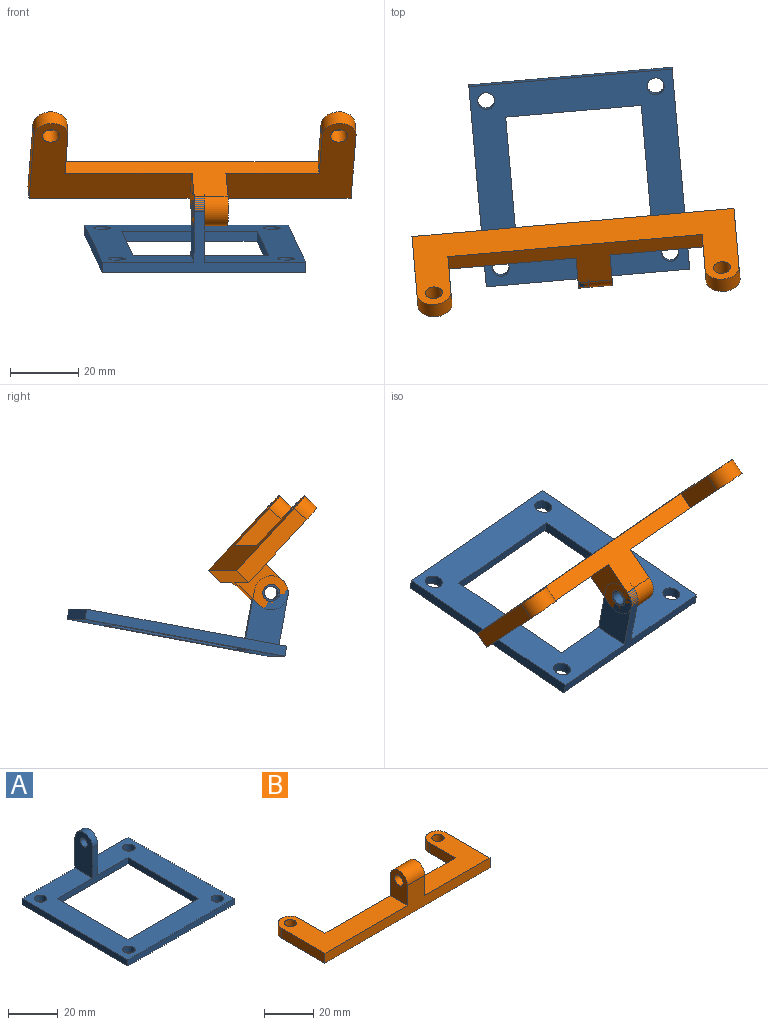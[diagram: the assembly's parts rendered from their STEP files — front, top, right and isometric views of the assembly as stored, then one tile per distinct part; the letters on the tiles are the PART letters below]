
ASSEMBLY  parts=2 mates=1
PART A: 18 faces, bbox 60x60x23 mm
  f0: plane 60x60mm, normal (0,0,1), area 1891.5mm2, adj f1,f2,f3,f4,f5,f6,f7,f8
  f1: plane 60x18mm, normal (0,1,0), area 225mm2, adj f0,f2,f8,f9,f10,f11,f12
  f2: plane 60x3mm, normal (-1,0,0), area 180mm2, adj f0,f1,f3,f9
  f3: plane 60x3mm, normal (0,-1,0), area 180mm2, adj f0,f2,f8,f9
  f4: plane 40x3mm, normal (1,0,0), area 120mm2, adj f0,f5,f7,f9
  f5: plane 40x18mm, normal (0,-1,0), area 165mm2, adj f0,f4,f6,f9,f10,f11,f12
  f6: plane 40x3mm, normal (-1,0,0), area 120mm2, adj f0,f5,f7,f9
  f7: plane 40x3mm, normal (0,1,0), area 120mm2, adj f0,f4,f6,f9
  f8: plane 60x3mm, normal (1,0,0), area 180mm2, adj f0,f1,f3,f9
  f9: plane 60x60mm, normal (0,0,-1), area 1921.5mm2, adj f1,f2,f3,f4,f5,f6,f7,f8
  f10: plane 20x10mm, normal (-1,0,0), area 176.7mm2, adj f0,f1,f5,f12,f13
  f11: plane 20x10mm, normal (1,0,0), area 176.7mm2, adj f0,f1,f5,f12,f13
  f12: cylinder r=5mm len=10mm, axis (1,0,0), area 47.1mm2, adj f1,f5,f10,f11
  f13: cylinder r=2mm len=4mm, axis (-1,0,0), area 37.7mm2, adj f10,f11
  f14: cylinder r=2.5mm len=5mm, axis (0,0,1), area 47.1mm2, adj f0,f9
  f15: cylinder r=2.5mm len=5mm, axis (0,0,1), area 47.1mm2, adj f0,f9
  f16: cylinder r=2.5mm len=5mm, axis (0,0,1), area 47.1mm2, adj f0,f9
  f17: cylinder r=2.5mm len=5mm, axis (0,0,1), area 47.1mm2, adj f0,f9
PART B: 17 faces, bbox 95x30x20 mm
  f0: plane 47.5x30mm, normal (0,0,1), area 644.6mm2, adj f1,f2,f5,f6,f9,f11,f14
  f1: plane 25x5mm, normal (-1,0,0), area 125mm2, adj f0,f2,f8,f14
  f2: plane 95x15mm, normal (0,-1,0), area 575mm2, adj f0,f1,f3,f7,f8,f11,f12,f13
  f3: plane 25x5mm, normal (1,0,0), area 125mm2, adj f2,f7,f8,f15
  f4: plane 15x5mm, normal (-1,0,0), area 75mm2, adj f5,f7,f8,f15
  f5: plane 75x15mm, normal (0,1,0), area 475mm2, adj f0,f4,f6,f7,f8,f11,f12,f13
  f6: plane 15x5mm, normal (1,0,0), area 75mm2, adj f0,f5,f8,f14
  f7: plane 37.5x30mm, normal (0,0,1), area 544.6mm2, adj f2,f3,f4,f5,f10,f12,f15
  f8: plane 95x30mm, normal (0,0,-1), area 1289.3mm2, adj f1,f2,f3,f4,f5,f6,f9,f10
  f9: cylinder r=2.5mm len=5mm, axis (0,0,-1), area 78.5mm2, adj f0,f8
  f10: cylinder r=2.5mm len=5mm, axis (0,0,-1), area 78.5mm2, adj f7,f8
  f11: plane 15x10mm, normal (-1,0,0), area 119.6mm2, adj f0,f2,f5,f13,f16
  f12: plane 15x10mm, normal (1,0,0), area 119.6mm2, adj f2,f5,f7,f13,f16
  f13: cylinder r=5mm len=10mm, axis (1,0,0), area 157.1mm2, adj f2,f5,f11,f12
  f14: cylinder r=5mm len=10mm, axis (0,0,1), area 78.5mm2, adj f0,f1,f6,f8
  f15: cylinder r=5mm len=10mm, axis (0,0,1), area 78.5mm2, adj f3,f4,f7,f8
  f16: cylinder r=2.5mm len=10mm, axis (-1,0,0), area 157.1mm2, adj f11,f12
PLACE A rot(axis=(0,0.09,-1),175deg) t=(1.95,46.69,44.91)mm
PLACE B rot(axis=(1,0.04,0.02),133deg) t=(0.73,26.22,71.98)mm
MATE revolute A.f12 <-> B.f13  axis (-1,-0.09,0) through (1.39,18.69,58.09)mm
